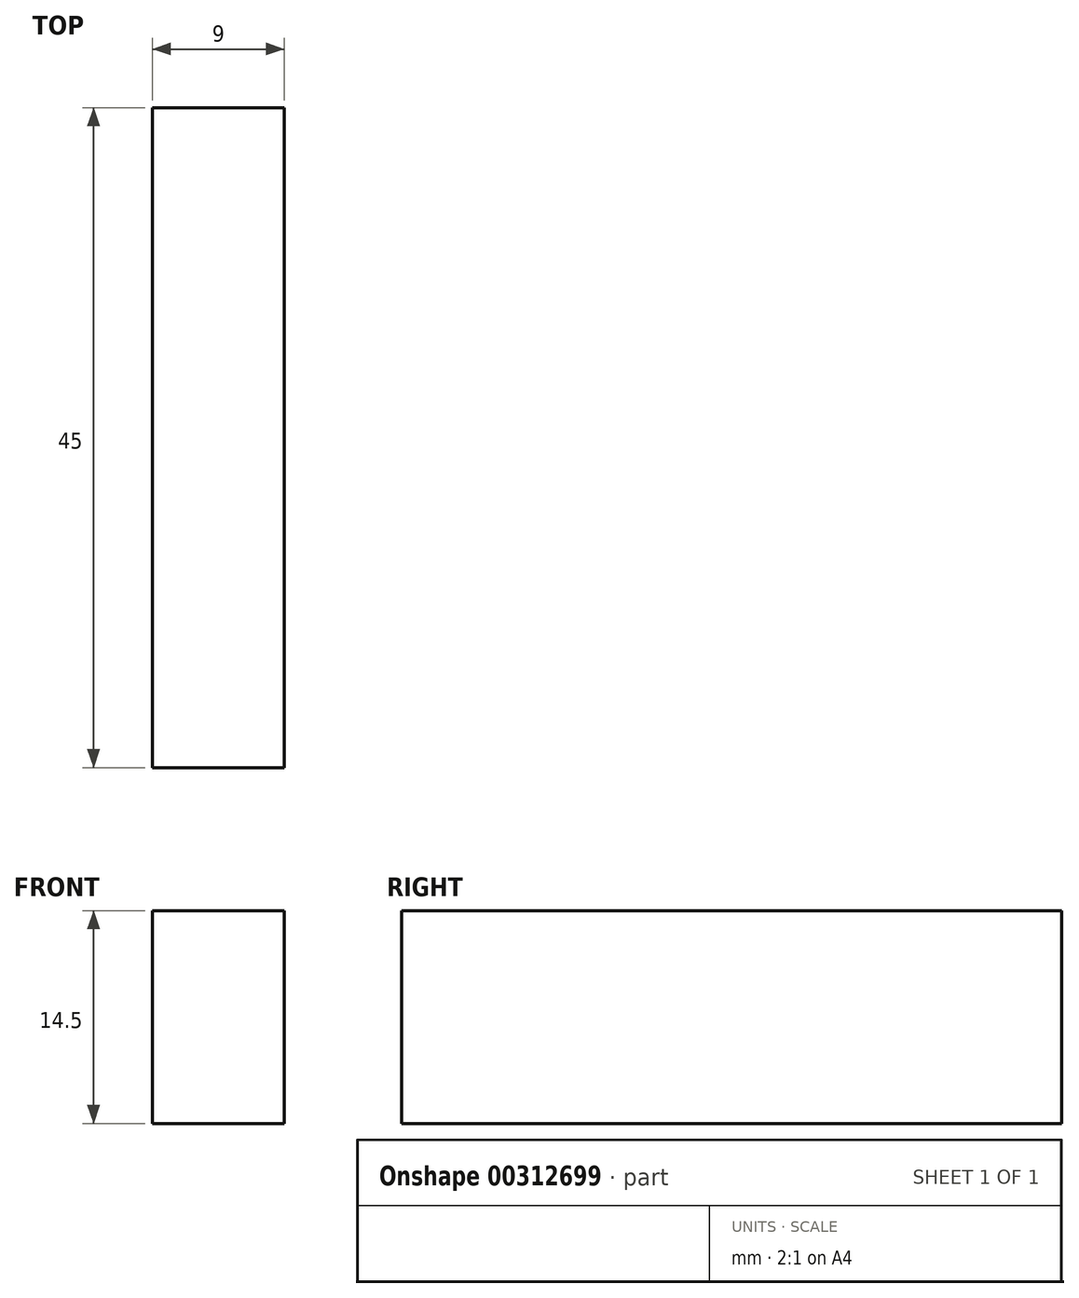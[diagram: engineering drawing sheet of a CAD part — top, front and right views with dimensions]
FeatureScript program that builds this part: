
annotation { "Feature Type Name" : "Feature", "Feature Type Description" : "" }
export const myFeature = defineFeature(function(context is Context, id is Id, definition is map)
    precondition{}
    {
        {
            var Q0;
            Q0=qCreatedBy(makeId("Top.planeOp"),FACE);
            var sketch = newSketch(context, id + "F0", { "sketchPlane" : qUnion([Q0])});
            skLineSegment(sketch, "E0.bottom", {"start": v(25.03, 16.2) * mm, "end": v(34.03, 16.2) * mm});
            skLineSegment(sketch, "E0.top", {"start": v(25.03, -28.8) * mm, "end": v(34.03, -28.8) * mm});
            skLineSegment(sketch, "E0.left", {"start": v(25.03, 16.2) * mm, "end": v(25.03, -28.8) * mm});
            skLineSegment(sketch, "E0.right", {"start": v(34.03, 16.2) * mm, "end": v(34.03, -28.8) * mm});
            skSolve(sketch);
        }
        {
            var Q0;
            Q0=makeQuery(id+"F0.imprint","IMPRINT",FACE,{"disambiguationData":[TD([[makeQuery(id+"F0.imprint","IMPRINT",EDGE,{"derivedFrom":sQuery(id+"F0.wireOp",EDGE,"E0.bottom")}),-1.0]])]});
            extrude(context, id + "F1", {"entities" : qUnion([Q0]), "depth" : 14.5 * mm});
        }
    });
